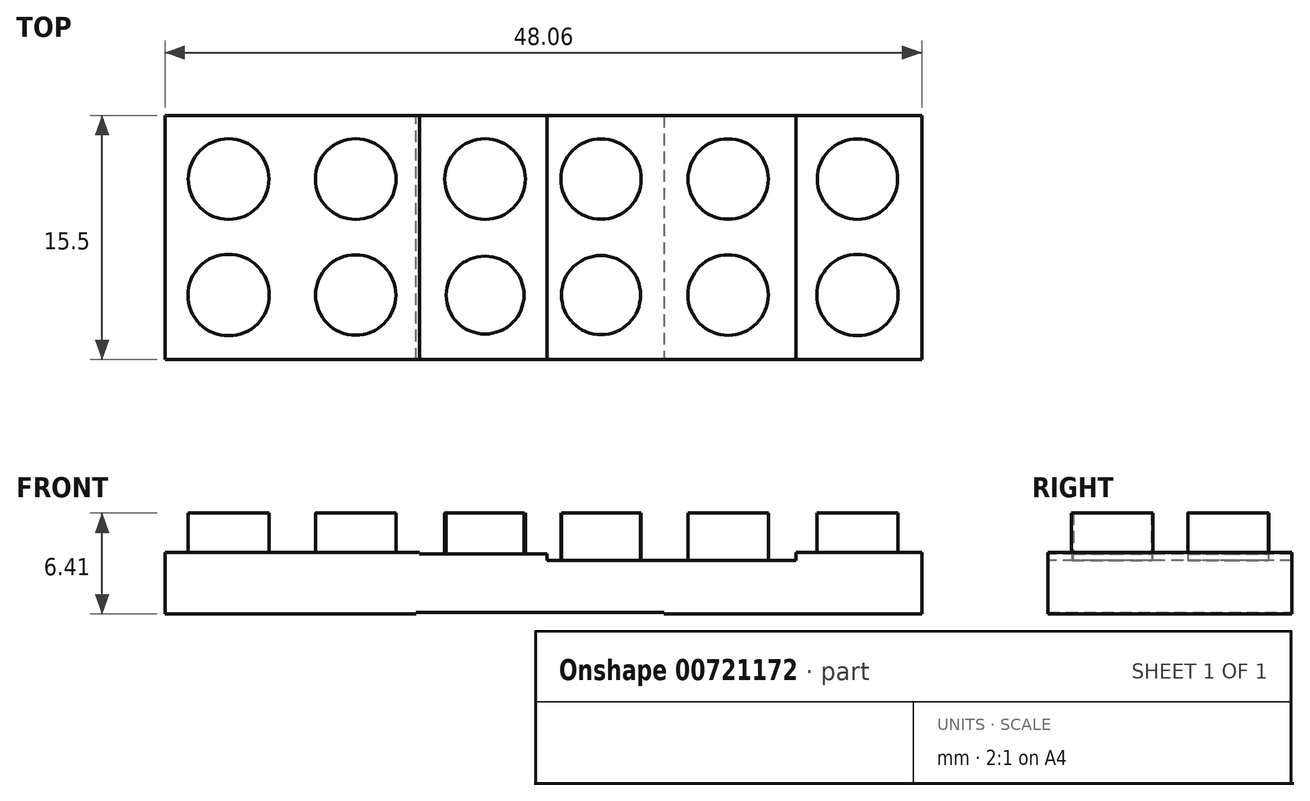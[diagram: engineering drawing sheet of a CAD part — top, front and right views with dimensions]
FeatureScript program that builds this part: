
annotation { "Feature Type Name" : "Feature", "Feature Type Description" : "" }
export const myFeature = defineFeature(function(context is Context, id is Id, definition is map)
    precondition{}
    {
        {
            var Q0;
            Q0=qCreatedBy(makeId("Front.planeOp"),FACE);
            var sketch = newSketch(context, id + "F0", { "sketchPlane" : qUnion([Q0])});
            skLineSegment(sketch, "E0", {"start": v(-25.76, 0) * mm, "end": v(22.3, 0) * mm});
            skLineSegment(sketch, "E1", {"start": v(22.3, 0) * mm, "end": v(22.3, 3.3) * mm});
            skLineSegment(sketch, "E2", {"start": v(22.3, 3.3) * mm, "end": v(-25.76, 3.3) * mm});
            skLineSegment(sketch, "E3", {"start": v(-25.76, 3.3) * mm, "end": v(-25.76, 0) * mm});
            skSolve(sketch);
        }
        {
            var Q0;
            Q0 = qSketchRegion(id + "F0", true);
            extrude(context, id + "F1", {"entities" : qUnion([Q0]), "depth" : 15.5 * mm, "offsetDistance" : 25 * mm});
        }
        {
            var Q0;
            Q0=makeQuery(id+"F1.opExtrude","SWEPT_FACE",FACE,{"disambiguationData":[OSD([sQuery(id+"F0.wireOp",EDGE,"E2")])]});
            var sketch = newSketch(context, id + "F2", { "sketchPlane" : qUnion([Q0])});
            skCircle(sketch, "E4", {"center": v(-21.73, -4.04) * mm, "radius": 2.57 * mm});
            skCircle(sketch, "E5", {"center": v(-21.73, -11.4) * mm, "radius": 2.58 * mm});
            skCircle(sketch, "E6", {"center": v(-13.66, -11.4) * mm, "radius": 2.55 * mm});
            skCircle(sketch, "E7", {"center": v(-13.66, -4.04) * mm, "radius": 2.57 * mm});
            skCircle(sketch, "E8", {"center": v(-5.44, -4.04) * mm, "radius": 2.57 * mm});
            skCircle(sketch, "E9", {"center": v(-5.44, -11.4) * mm, "radius": 2.47 * mm});
            skCircle(sketch, "E10", {"center": v(1.92, -11.4) * mm, "radius": 2.5 * mm});
            skCircle(sketch, "E11", {"center": v(1.92, -4.04) * mm, "radius": 2.55 * mm});
            skCircle(sketch, "E12", {"center": v(10, -4.04) * mm, "radius": 2.55 * mm});
            skCircle(sketch, "E13", {"center": v(10, -11.4) * mm, "radius": 2.55 * mm});
            skCircle(sketch, "E14", {"center": v(18.21, -11.4) * mm, "radius": 2.58 * mm});
            skCircle(sketch, "E15", {"center": v(18.21, -4.04) * mm, "radius": 2.55 * mm});
            skLineSegment(sketch, "E16", {"start": v(5.77, 0) * mm, "end": v(5.77, -15.5) * mm});
            skLineSegment(sketch, "E17", {"start": v(-9.4, -15.5) * mm, "end": v(-9.4, 0) * mm});
            skSolve(sketch);
        }
        {
            var Q0;
            Q0 = qSketchRegion(id + "F2", true);
            extrude(context, id + "F3", {"entities" : qUnion([Q0]), "operationType" : NewBodyOperationType.ADD, "depth" : 3 * mm, "offsetDistance" : 25 * mm});
        }
        {
            var Q0;
            Q0=makeQuery(id+"F1.opExtrude","SWEPT_FACE",FACE,{"disambiguationData":[OSD([sQuery(id+"F0.wireOp",EDGE,"E0")])]});
            var sketch = newSketch(context, id + "F4", { "sketchPlane" : qUnion([Q0])});
            skPoint(sketch, "E18", {"position": v(-9.82, 0) * mm});
            skPoint(sketch, "E19", {"position": v(5.93, 0) * mm});
            skLineSegment(sketch, "E20", {"start": v(5.93, 0) * mm, "end": v(5.93, 15.5) * mm});
            skLineSegment(sketch, "E21", {"start": v(5.93, 15.5) * mm, "end": v(22.3, 15.5) * mm});
            skLineSegment(sketch, "E22", {"start": v(22.3, 15.5) * mm, "end": v(22.3, 0) * mm});
            skLineSegment(sketch, "E23", {"start": v(22.3, 0) * mm, "end": v(5.93, 0) * mm});
            skLineSegment(sketch, "E24", {"start": v(-9.82, 0) * mm, "end": v(-25.76, 0) * mm});
            skLineSegment(sketch, "E25", {"start": v(-25.76, 0) * mm, "end": v(-25.76, 15.5) * mm});
            skLineSegment(sketch, "E26", {"start": v(-25.76, 15.5) * mm, "end": v(-9.82, 15.5) * mm});
            skLineSegment(sketch, "E27", {"start": v(-9.82, 15.5) * mm, "end": v(-9.82, 0) * mm});
            skSolve(sketch);
        }
        {
            var Q0;
            Q0 = qSketchRegion(id + "F4", true);
            extrude(context, id + "F5", {"entities" : qUnion([Q0]), "operationType" : NewBodyOperationType.ADD, "depth" : .1 * mm, "offsetDistance" : 25 * mm});
        }
        {
            var Q0;
            Q0=makeQuery(id+"F1.opExtrude","SWEPT_FACE",FACE,{"disambiguationData":[OSD([sQuery(id+"F0.wireOp",EDGE,"E2")])]});
            var sketch = newSketch(context, id + "F6", { "sketchPlane" : qUnion([Q0])});
            skLineSegment(sketch, "E28", {"start": v(-9.6, 0) * mm, "end": v(-9.6, -15.5) * mm});
            skLineSegment(sketch, "E29", {"start": v(-9.6, -15.5) * mm, "end": v(-25.76, -15.5) * mm});
            skLineSegment(sketch, "E30", {"start": v(-25.76, -15.5) * mm, "end": v(-25.76, 0) * mm});
            skLineSegment(sketch, "E31", {"start": v(-25.76, 0) * mm, "end": v(-9.6, 0) * mm});
            skLineSegment(sketch, "E32", {"start": v(22.3, -15.5) * mm, "end": v(22.3, 0) * mm});
            skLineSegment(sketch, "E33", {"start": v(22.3, 0) * mm, "end": v(14.3, 0) * mm});
            skLineSegment(sketch, "E34", {"start": v(14.3, 0) * mm, "end": v(14.3, -15.5) * mm});
            skLineSegment(sketch, "E35", {"start": v(14.3, -15.5) * mm, "end": v(22.3, -15.5) * mm});
            skSolve(sketch);
        }
        {
            var Q0;
            Q0 = qSketchRegion(id + "F6", true);
            extrude(context, id + "F7", {"entities" : qUnion([Q0]), "operationType" : NewBodyOperationType.ADD, "depth" : .5 * mm, "offsetDistance" : 25 * mm});
        }
        {
            var Q0;
            Q0=makeQuery(id+"F1.opExtrude","SWEPT_FACE",FACE,{"disambiguationData":[OSD([sQuery(id+"F0.wireOp",EDGE,"E2")])]});
            var sketch = newSketch(context, id + "F8", { "sketchPlane" : qUnion([Q0])});
            skLineSegment(sketch, "E36", {"start": v(-1.5, 0) * mm, "end": v(-1.5, -15.5) * mm});
            skLineSegment(sketch, "E37", {"start": v(-1.5, -15.5) * mm, "end": v(-9.6, -15.5) * mm});
            skLineSegment(sketch, "E38", {"start": v(-9.6, -15.5) * mm, "end": v(-9.6, 0) * mm});
            skLineSegment(sketch, "E39", {"start": v(-9.6, 0) * mm, "end": v(-1.5, 0) * mm});
            skSolve(sketch);
        }
        {
            var Q0;
            Q0 = qSketchRegion(id + "F8", true);
            extrude(context, id + "F9", {"entities" : qUnion([Q0]), "operationType" : NewBodyOperationType.ADD, "depth" : .4 * mm, "offsetDistance" : 25 * mm});
        }
    });
